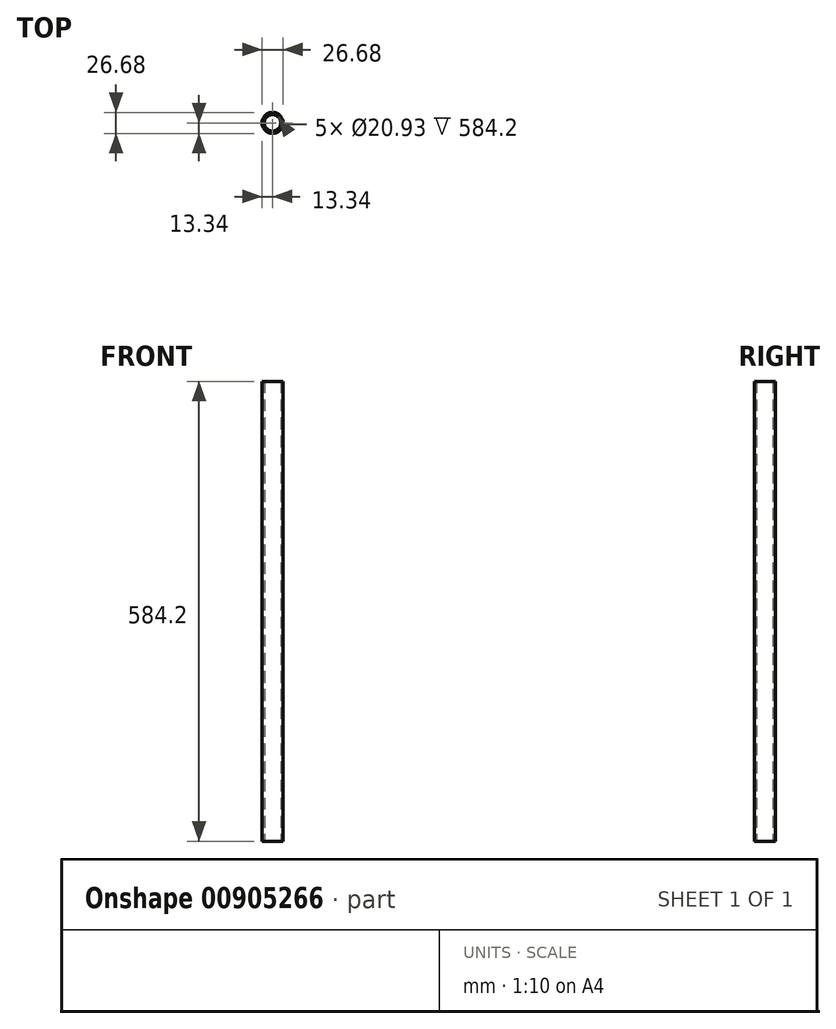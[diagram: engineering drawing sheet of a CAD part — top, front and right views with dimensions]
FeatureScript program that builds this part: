
annotation { "Feature Type Name" : "Feature", "Feature Type Description" : "" }
export const myFeature = defineFeature(function(context is Context, id is Id, definition is map)
    precondition{}
    {
        {
            var Q0;
            Q0=qCreatedBy(makeId("Top.planeOp"),FACE);
            var sketch = newSketch(context, id + "F0", { "sketchPlane" : qUnion([Q0])});
            skCircle(sketch, "E0", {"center": v(0, 0) * mm, "radius": 13.34 * mm});
            skCircle(sketch, "E1", {"center": v(0, 0) * mm, "radius": 10.46 * mm});
            skSolve(sketch);
        }
        {
            var Q0;
            Q0=qSketchRegion(id+"F0",true);
            extrude(context, id + "F1", {"entities" : qUnion([Q0]), "depth" : 584.2 * mm, "offsetDistance" : 25.4 * mm});
        }
    });
